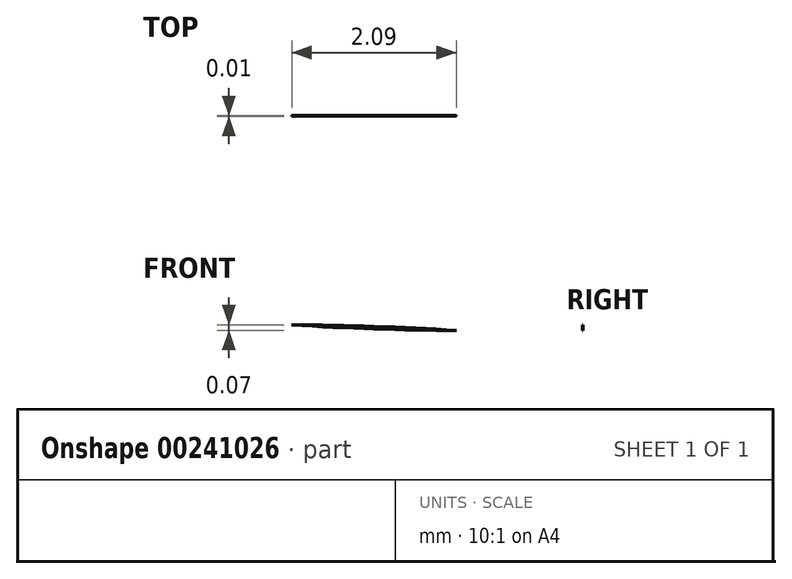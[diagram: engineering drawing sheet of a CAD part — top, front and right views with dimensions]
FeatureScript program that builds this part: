
annotation { "Feature Type Name" : "Feature", "Feature Type Description" : "" }
export const myFeature = defineFeature(function(context is Context, id is Id, definition is map)
    precondition{}
    {
        {
            var Q0;
            Q0=qCreatedBy(makeId("Front.planeOp"),FACE);
            var sketch = newSketch(context, id + "F0", { "sketchPlane" : qUnion([Q0])});
            skCircle(sketch, "E0", {"center": v(0, 0) * mm, "radius": 44.45 * mm});
            skLineSegment(sketch, "E1", {"start": v(0, 0) * mm, "end": v(76.2, 0) * mm});
            skLineSegment(sketch, "E2", {"start": v(76.2, 0) * mm, "end": v(-76.2, 0) * mm});
            skCircle(sketch, "E3", {"center": v(76.2, 0) * mm, "radius": 12.7 * mm});
            skCircle(sketch, "E4", {"center": v(-76.2, 0) * mm, "radius": 12.7 * mm});
            skLineSegment(sketch, "E5", {"start": v(0, 0) * mm, "end": v(0, -63.5) * mm});
            skLineSegment(sketch, "E6", {"start": v(76.2, 0) * mm, "end": v(107.95, 0) * mm});
            skLineSegment(sketch, "E7", {"start": v(0, 0) * mm, "end": v(0, 63.5) * mm});
            skLineSegment(sketch, "E8", {"start": v(-76.2, 0) * mm, "end": v(-107.95, 0) * mm});
            skSolve(sketch);
        }
        {
            var Q0;
            Q0=qCreatedBy(makeId("Front.planeOp"),FACE);
            var sketch = newSketch(context, id + "F1", { "sketchPlane" : qUnion([Q0])});
            skArc(sketch, "E9", {"start": v(-73.86, 31.79) * mm, "mid": v(-107.7, 0.2) * mm, "end": v(-74.02, -31.58) * mm});
            skArc(sketch, "E10", {"start": v(74.45, -31.4) * mm, "mid": v(107.83, 1.41) * mm, "end": v(72.23, 31.81) * mm});
            skArc(sketch, "E11", {"start": v(47.28, 42.4) * mm, "mid": v(0, 63.5) * mm, "end": v(-47.28, 42.4) * mm});
            skArc(sketch, "E12.trimOffspring", {"start": v(-47.5, -42.15) * mm, "mid": v(-1.95, -63.47) * mm, "end": v(44.82, -44.98) * mm});
            skArc(sketch, "E13", {"start": v(-75.95, 31.86) * mm, "mid": v(-58.85, 34.78) * mm, "end": v(-44.82, 44.98) * mm});
            skArc(sketch, "E14", {"start": v(-44.82, -44.98) * mm, "mid": v(-58.82, -34.66) * mm, "end": v(-75.95, -31.64) * mm});
            skArc(sketch, "E15.MirrorCS", {"start": v(75.95, 31.86) * mm, "mid": v(58.85, 34.78) * mm, "end": v(44.82, 44.98) * mm});
            skArc(sketch, "E16.MirrorCS", {"start": v(44.82, -44.98) * mm, "mid": v(46.12, -43.53) * mm, "end": v(47.5, -42.15) * mm});
            skArc(sketch, "E17.trimOffspring", {"start": v(47.5, -42.15) * mm, "mid": v(47.6, -42.02) * mm, "end": v(47.72, -41.9) * mm});
            skArc(sketch, "E18", {"start": v(75.78, -31.45) * mm, "mid": v(58.71, -34.59) * mm, "end": v(44.82, -44.98) * mm});
            skLineSegment(sketch, "E19", {"start": v(-75.95, 0.1) * mm, "end": v(0, 0) * mm});
            skSolve(sketch);
        }
        {
            var Q0;
            {var subQ1=sQuery(id+"F1.wireOp",EDGE,"E9");var subQ6=sQuery(id+"F1.wireOp",EDGE,"E13");var subQ16=makeQuery(id+"F1.imprint","INTERSECT",VERTEX,{"disambiguationData":[OD(1.0)],"derivedFrom":[subQ1,subQ6]});Q0=makeQuery(id+"F1.imprint","IMPRINT",FACE,{"disambiguationData":[TD([[makeQuery(id+"F1.imprint","IMPRINT",EDGE,{"disambiguationData":[TD([[subQ16,-1.0]])],"derivedFrom":subQ1}),1.0]])]});}
            extrude(context, id + "F2", {"entities" : qUnion([Q0]), "depth" : 1 / 101.6 * mm});
        }
        {
            var Q0;
            Q0=sQuery(id+"F0.wireOp",VERTEX,"E8.start");
            var Q1;
            Q1=sQuery(id+"F0.wireOp",VERTEX,"E6.start");
            var Q2;
            Q2=makeQuery(id+"F2.opExtrude","SWEPT_BODY",BODY,{"disambiguationData":[OSD([sQuery(id+"F1.wireOp",EDGE,"E9"),sQuery(id+"F1.wireOp",EDGE,"E10"),sQuery(id+"F1.wireOp",EDGE,"E11"),sQuery(id+"F1.wireOp",EDGE,"E12.trimOffspring"),sQuery(id+"F1.wireOp",EDGE,"E13"),sQuery(id+"F1.wireOp",EDGE,"E14"),sQuery(id+"F1.wireOp",EDGE,"E15.MirrorCS"),sQuery(id+"F1.wireOp",EDGE,"E18")])]});
            hole(context, id + "F3", {"style" : HoleStyle.SIMPLE, "endStyle" : HoleEndStyle.THROUGH, "oppositeDirection" : true, "holeDiameter" : 25.4 * mm, "locations" : qUnion([Q0, Q1]), "scope" : qUnion([Q2]), "isTappedThrough" : true});
        }
        {
            var Q0;
            Q0=sQuery(id+"F0.wireOp",VERTEX,"E0.center");
            var Q1;
            Q1=makeQuery(id+"F2.opExtrude","SWEPT_BODY",BODY,{"disambiguationData":[OSD([sQuery(id+"F1.wireOp",EDGE,"E9"),sQuery(id+"F1.wireOp",EDGE,"E10"),sQuery(id+"F1.wireOp",EDGE,"E11"),sQuery(id+"F1.wireOp",EDGE,"E12.trimOffspring"),sQuery(id+"F1.wireOp",EDGE,"E13"),sQuery(id+"F1.wireOp",EDGE,"E14"),sQuery(id+"F1.wireOp",EDGE,"E15.MirrorCS"),sQuery(id+"F1.wireOp",EDGE,"E18")])]});
            hole(context, id + "F4", {"style" : HoleStyle.SIMPLE, "endStyle" : HoleEndStyle.THROUGH, "oppositeDirection" : true, "holeDiameter" : 88.9 * mm, "locations" : qUnion([Q0]), "scope" : qUnion([Q1]), "isTappedThrough" : true});
        }
    });
